# Revit family: SDCF8X200
name_source: partatom
category: Detail Items
revit_build: Autodesk Revit 2015 (Build: 20140606_1530(x64)
units: mm (PartAtom-declared; Revit-internal decimal feet)

## types (2) — shared parameters
Density = 0.00 kg
Description = 0233893899292358545357972904618716474256
EPD = 0.04
ETA / DoP = https://www.strongtie.eu
Manufacturer = Simpson Strong-Tie
Model = SDCF8X200
Model Disclaimer = Contact Simpson Strong-Tie Company  for more information
Model ID = Simpson Strong-Tie
Name = SDCF8X200
ObjectType = SDCF8X200
Product Material = E-coat®
Product Type = 0233893899292358545357972904618716474256
Reference = SDCF8X200
Technical datasheet = https://www.strongtie.eu
URL = www.strongtie.eu
UniClass Number = Wood screws
UniClass Title = Joist hangers

## per-type parameters (varying)
| type | _visiblefront | _visibletop |
| SST_SDCF8X200_Front | Yes | No |
| SST_SDCF8X200_Top | No | Yes |

## geometry (parser evidence)
native form markers: Sweep x1
no freeform markers — native parametric forms only
